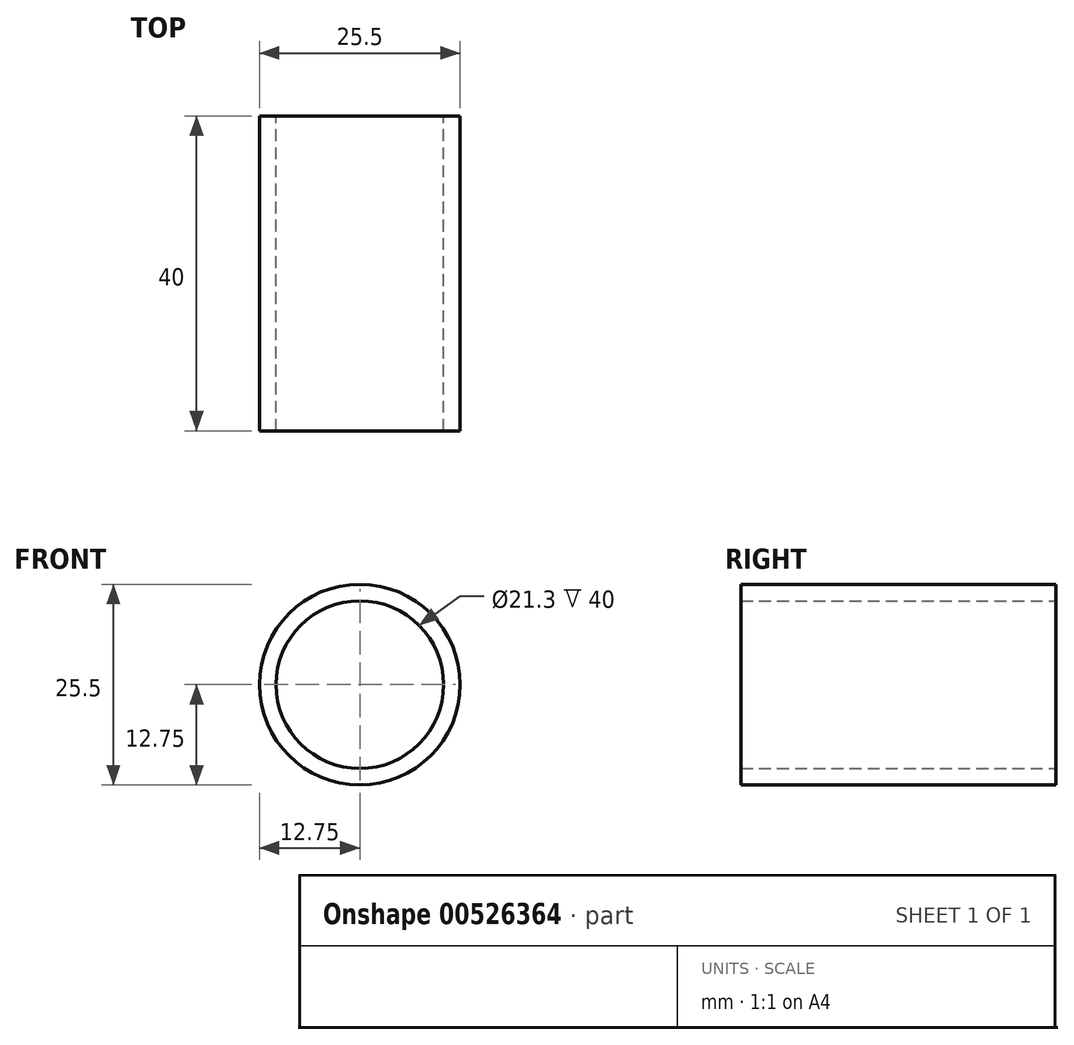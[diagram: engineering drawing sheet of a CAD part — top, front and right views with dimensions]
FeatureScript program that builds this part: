
annotation { "Feature Type Name" : "Feature", "Feature Type Description" : "" }
export const myFeature = defineFeature(function(context is Context, id is Id, definition is map)
    precondition{}
    {
        {
            var Q0;
            Q0=qCreatedBy(makeId("Front.planeOp"),FACE);
            var sketch = newSketch(context, id + "F0", { "sketchPlane" : qUnion([Q0])});
            skCircle(sketch, "E0", {"center": v(0, 0) * mm, "radius": 12.75 * mm});
            skCircle(sketch, "E1", {"center": v(0, 0) * mm, "radius": 10.65 * mm});
            skSolve(sketch);
        }
        {
            var Q0;
            Q0 = qSketchRegion(id + "F0", true);
            extrude(context, id + "F1", {"entities" : qUnion([Q0]), "depth" : 40 * mm, "offsetDistance" : 25 * mm});
        }
    });
